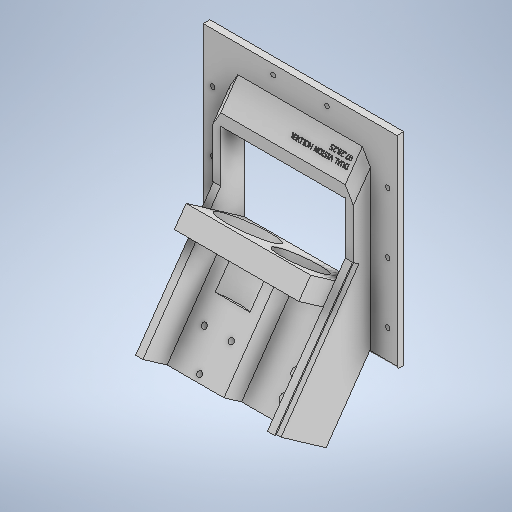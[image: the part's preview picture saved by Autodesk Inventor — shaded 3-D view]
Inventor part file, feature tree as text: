
AUTODESK INVENTOR PART (.ipt)
format: ipt  version: 2025.2 (Build 292293000, 293)  size: 1,334,272 bytes
history: native  units: in
note: dims shown in document units (in); Inventor stores cm internally (conversion verified against a paired STEP export)
features: sketch x42, extrude x37, plane x5, projected_geometry x3, move_body x1, chamfer x1, fillet x1, hole x1
ambient origin geometry x8: Origin, YZ Plane, XZ Plane, XY Plane, X Axis, Y Axis, Z Axis, Center Point
bodies: Solid1 (feature_tree)
feature tree (91):
  extrude  "Extrusion1"  Depth=0.1969in TaperAngle=0.0deg
  move_body  "Move Body1"
  plane  "Work Plane1"
  sketch  "Sketch5"  dims[d5=1.7717in d6=1.7717in d7=1.7717in d8=1.7717in d9=0.8108in d10=90.0deg d11=0.0787in d12=0.3701in d13=0.4252in d14=0.1362in d15=-0.0984in d16=-0.0591in d17=0.0in]
  plane  "Work Plane2"
  extrude  "Extrusion4"  TaperAngle=0.0deg  [1 undecoded]
  extrude  "Extrusion6"  Depth=0.2405in
  extrude  "Extrusion8"  Depth=2.5591in TaperAngle=0.0deg
  chamfer  "Chamfer1"  [1 undecoded]
  extrude  "Extrusion11"  Depth=0.2362in
  plane  "Work Plane3"
  extrude  "Extrusion13"  Depth=0.1969in TaperAngle=0.0deg
  plane  "Work Plane4"
  plane  "Work Plane6"
  extrude  "Extrusion21"  Depth=0.5027in
  extrude  "Extrusion22"  Depth=0.5027in
  extrude  "Extrusion25"  Depth=1.1811in TaperAngle=0.0deg
  extrude  "Extrusion26"  Depth=0.1969in
  sketch  "Sketch33"  dims[d100=3.6403in d101=2.7717in]
  extrude  "Extrusion27"  Depth=0.2362in TaperAngle=0.0deg
  extrude  "Extrusion29"  Depth=3.6403in
  extrude  "Extrusion28"  Depth=0.6299in TaperAngle=0.0deg
  sketch  "Sketch36"  dims[d124=0.9712in d125=0.0in d126=0.5906in d127=0.0in d128=11.3469in d129=0.0in]
  extrude  "Extrusion30"  Depth=0.7874in
  extrude  "Extrusion31"  Depth=0.5906in TaperAngle=0.0deg
  sketch  "Sketch39"  dims[d149=0.2756in d150=0.0in d151=0.0in]
  fillet  "Fillet1"  Radius=11.3469in
  extrude  "Extrusion33"  Depth=0.6299in
  extrude  "Extrusion34"  Depth=0.2756in
  extrude  "Extrusion35"  TaperAngle=0.0deg  [1 undecoded]
  sketch  "Sketch45"  dims[d170=4.7244in d171=0.0in d174=0.0in d175=0.0in]
  extrude  "Extrusion37"  Depth=0.1181in TaperAngle=0.0deg
  extrude  "Extrusion38"  Depth=0.1181in TaperAngle=0.0deg
  extrude  "Extrusion40"  Depth=0.1181in TaperAngle=0.0deg
  extrude  "Extrusion41"  TaperAngle=0.0deg  [1 undecoded]
  extrude  "Extrusion43"  TaperAngle=0.0deg  [1 undecoded]
  extrude  "Extrusion44"  TaperAngle=0.0deg  [1 undecoded]
  extrude  "Extrusion46"  Depth=0.4724in
  extrude  "Extrusion47"  Depth=0.0394in TaperAngle=0.0deg
  extrude  "Extrusion48"  Depth=3.9671in TaperAngle=0.0deg
  sketch  "Sketch61"  dims[d253=60.0deg d254=0.3937in]
  extrude  "Extrusion50"  Depth=0.1969in
  extrude  "Extrusion51"  TaperAngle=60.0deg  [1 undecoded]
  extrude  "Extrusion52"  Depth=0.1969in
  extrude  "Extrusion53"  Depth=0.3937in
  extrude  "Extrusion54"  Depth=0.3937in
  extrude  "Extrusion57"  Depth=0.1181in TaperAngle=0.0deg
  extrude  "Extrusion59"  Depth=0.3937in TaperAngle=0.0deg
  extrude  "Extrusion60"  TaperAngle=0.0deg  [1 undecoded]
  extrude  "Extrusion61"  Depth=1.0236in
  extrude  "Extrusion62"  TaperAngle=0.0deg  [1 undecoded]
  sketch  "Sketch1"  dims[d1=0.5512in d2=0.1969in d3=0.0in]
  sketch  "Sketch6"  dims[d18=0.2749in d24=0.2405in]
  sketch  "Sketch8"  dims[d25=2.7559in d26=0.0in d29=2.5591in d30=0.0in d36=0.0in d37=0.0in]
  sketch  "Sketch12"  dims[d42=0.2362in d43=0.2362in]
  sketch  "Sketch15"  dims[d52=0.2362in d53=0.0787in d54=45.0deg d55=0.1969in d56=0.0in]
  sketch  "Sketch17"  dims[d59=0.5906in d60=0.0in d76=0.5027in]
  sketch  "Sketch27"  dims[d77=0.5027in d78=0.5027in]
  sketch  "Sketch28"  dims[d79=0.5027in d81=1.1811in d82=0.0in]
  sketch  "Sketch31"  dims[d83=0.0in d84=0.0in d91=0.1969in]
  sketch  "Sketch32"  dims[d94=0.2362in d95=0.0in d96=0.2362in d97=0.0in]
  sketch  "Sketch34"  dims[d112=1.9685in d113=0.6299in d114=0.0in]
  sketch  "Sketch35"  dims[d115=0.1575in d117=0.1575in d122=0.7874in d123=0.9331in]
  sketch  "Sketch37"  dims[d130=11.3469in d131=0.0in d141=0.6299in]
  sketch  "Sketch38"  dims[d142=0.0787in d147=0.2756in]
  sketch  "Sketch41"  dims[d154=0.1181in d155=0.0in d156=0.1181in d157=0.0in]
  sketch  "Sketch42"  dims[d158=0.4724in d160=0.1181in d161=0.0in]
  sketch  "Sketch44"  dims[d164=0.1181in d165=0.0in d168=0.5906in d169=0.0in]
  projected_geometry  "Projected Loop2"
  projected_geometry  "Projected Loop3"
  projected_geometry  "Projected Loop5"
  sketch  "Sketch47"  dims[d176=0.7313in d177=0.0in d186=0.0in d187=0.0in]
  sketch  "Sketch49"  dims[d188=0.0in d189=0.0in d194=0.0in d195=0.0in]
  sketch  "Sketch50"  dims[d196=0.5906in d197=0.4724in]
  sketch  "Sketch52"  dims[d198=0.0591in d199=0.0in d200=0.0394in d201=0.0in]
  sketch  "Sketch53"  dims[d235=6.1063in d236=0.0in d244=3.9671in d245=0.0in]
  sketch  "Sketch56"  dims[d246=0.9963in d248=0.1969in]
  sketch  "Sketch58"  dims[d249=0.1378in d250=60.0deg]
  sketch  "Sketch59"  dims[d251=0.1969in d252=0.1378in]
  sketch  "Sketch63"  dims[d255=0.3937in d256=0.3937in]
  sketch  "Sketch64"  dims[d257=0.1181in d258=0.0in d259=0.0787in d260=0.0in]
  sketch  "Sketch65"  dims[d261=1.9685in d262=0.0in d271=0.3937in d272=0.0in]
  sketch  "Sketch66"  dims[d275=0.3937in d276=0.0in d277=0.0in d278=0.0in]
  sketch  "Sketch67"  dims[d279=1.3386in d280=1.0236in]
  sketch  "Sketch70"  dims[d281=1.4764in d282=0.0in d283=0.0in]
  sketch  "Sketch72"  dims[d284=1.5748in d287=1.1614in]
  sketch  "Sketch75"  dims[d288=0.8512in]
  sketch  "Sketch76"  dims[d289=0.6299in d290=0.0in]
  sketch  "Sketch77"  dims[d38=0.0197in d39=0.0344in d57=0.0197in d58=0.0344in d159=0.0344in d178=0.0in d179=0.0in d180=0.0in d181=0.0in d202=0.0197in d203=0.0344in]
  sketch  "Sketch2"  dims[d4=0.315in]
  hole  "Hole1"  [1 undecoded]
note: 10 required parameter values undecoded (feature->parameter linkage not recoverable at this tier; creation-order binding heuristic only, values carry confidence <= 0.55)
